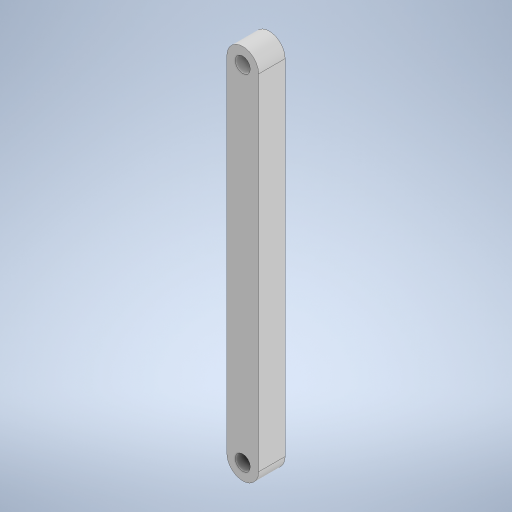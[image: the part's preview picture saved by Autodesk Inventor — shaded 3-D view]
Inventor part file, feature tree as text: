
AUTODESK INVENTOR PART (.ipt)
format: ipt  version: 2023 (Build 270158000, 158)  size: 242,688 bytes
history: native  units: mm
features: extrude x1, sketch x1
ambient origin geometry x8: Origin, YZ Plane, XZ Plane, XY Plane, X Axis, Y Axis, Z Axis, Center Point
bodies: Solid1 (feature_tree)
feature tree (2):
  extrude  "Extrusion1"  Depth=6.0mm
  sketch  "Sketch1"  dims[d8=5.0mm d9=0.0mm d10=6.0mm d11=71.0mm d12=3.0mm d13=6.0mm d14=2.85mm d15=3.0mm d16=6.0mm d17=2.85mm]
